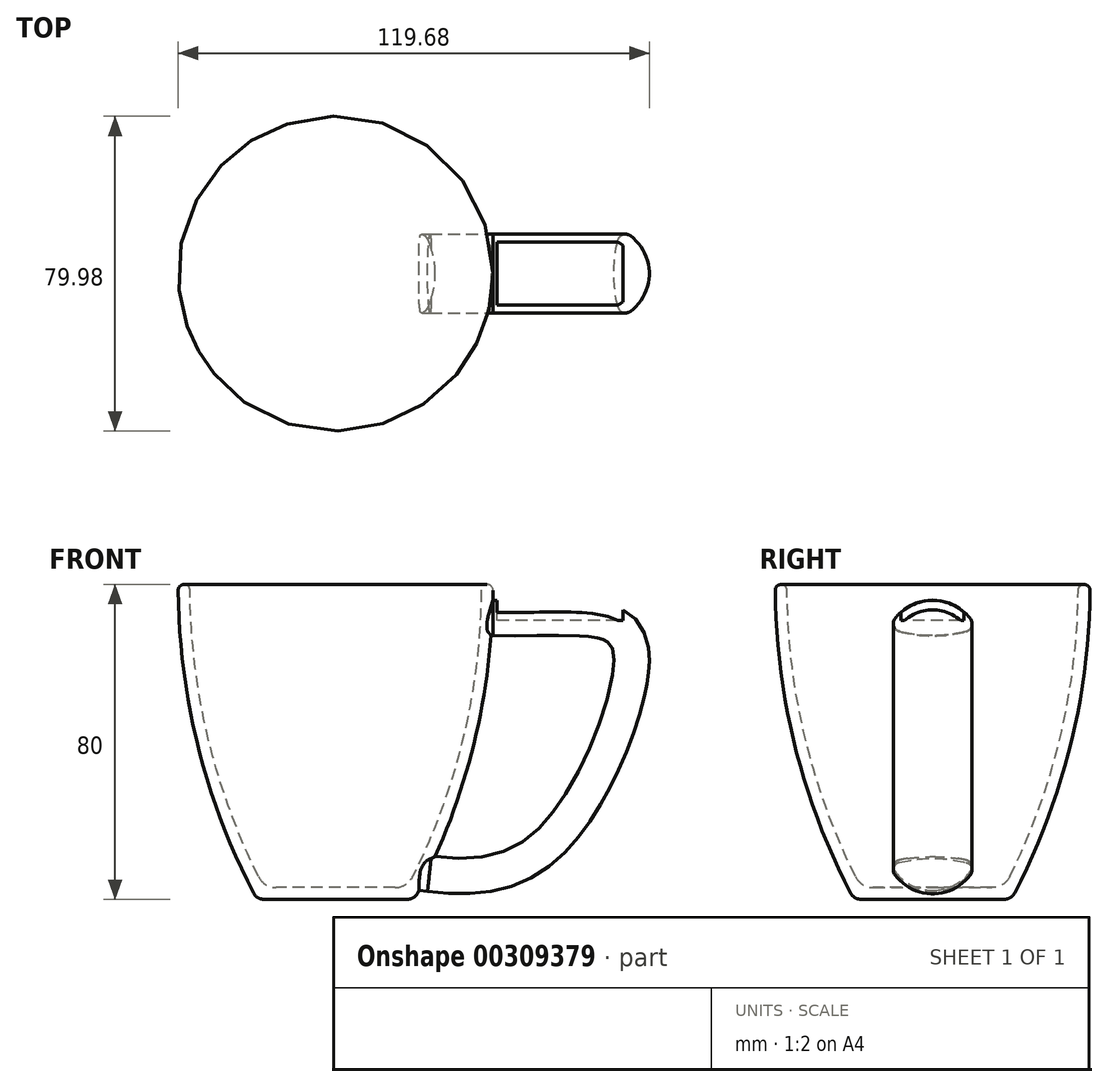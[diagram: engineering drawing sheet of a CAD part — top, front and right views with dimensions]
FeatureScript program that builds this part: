
annotation { "Feature Type Name" : "Feature", "Feature Type Description" : "" }
export const myFeature = defineFeature(function(context is Context, id is Id, definition is map)
    precondition{}
    {
        {
            var Q0;
            Q0=qCreatedBy(makeId("Front.planeOp"),FACE);
            var sketch = newSketch(context, id + "F0", { "sketchPlane" : qUnion([Q0])});
            skLineSegment(sketch, "E0", {"start": v(0, 3) * mm, "end": v(0, 0) * mm});
            skLineSegment(sketch, "E1", {"start": v(0, 0) * mm, "end": v(20, 0) * mm});
            skArc(sketch, "E2", {"start": v(20, 0) * mm, "mid": v(34.92, 38.77) * mm, "end": v(40, 80) * mm});
            skArc(sketch, "E3.0", {"start": v(18.19, 3) * mm, "mid": v(32.23, 40.37) * mm, "end": v(37, 80) * mm});
            skLineSegment(sketch, "E3.1", {"start": v(0, 3) * mm, "end": v(18.19, 3) * mm});
            skLineSegment(sketch, "E4", {"start": v(37, 80) * mm, "end": v(40, 80) * mm});
            skLineSegment(sketch, "E5", {"start": v(40, 160) * mm, "end": v(40, 0) * mm, "construction": true});
            skLineSegment(sketch, "E6", {"start": v(37, 160) * mm, "end": v(37, 0) * mm, "construction": true});
            skSolve(sketch);
        }
        {
            var Q0;
            Q0=qSketchRegion(id+"F0",true);
            var Q1;
            Q1=sQuery(id+"F0.wireOp",EDGE,"E0");
            revolve(context, id + "F1", {"entities" : qUnion([Q0]), "axis" : qUnion([Q1]), "revolveType" : RevolveType.FULL});
        }
        {
            var Q0;
            Q0=sQuery(id+"F0.wireOp",EDGE,"E5");
            cPlane(context, id + "F2", {"entities" : qUnion([Q0]), "cplaneType" : CPlaneType.LINE_ANGLE, "offset" : 150 * mm, "angle" : 0 * degree, "width" : 150 * mm, "height" : 150 * mm});
        }
        {
            var Q0;
            Q0=qCreatedBy(id+"F2.planeOp",FACE);
            var sketch = newSketch(context, id + "F3", { "sketchPlane" : qUnion([Q0])});
            skPoint(sketch, "E7", {"position": v(0, 70) * mm});
            skArc(sketch, "E8", {"start": v(9.6, 71.2) * mm, "mid": v(0, 76) * mm, "end": v(-9.6, 71.2) * mm});
            skArc(sketch, "E9", {"start": v(9.6, 71.2) * mm, "mid": v(9.89, 69.33) * mm, "end": v(8.5, 68.06) * mm});
            skArc(sketch, "E10", {"start": v(-9.6, 71.2) * mm, "mid": v(-9.89, 69.33) * mm, "end": v(-8.5, 68.06) * mm});
            skArc(sketch, "E11", {"start": v(-8.5, 68.06) * mm, "mid": v(0, 67) * mm, "end": v(8.5, 68.06) * mm});
            skSolve(sketch);
        }
        {
            var Q0;
            Q0=qSketchRegion(id+"F3",true);
            extrude(context, id + "F4", {"entities" : qUnion([Q0]), "operationType" : NewBodyOperationType.ADD, "endBound" : BoundingType.UP_TO_NEXT, "depth" : 25 * mm});
        }
        {
            var Q0;
            Q0=qCreatedBy(makeId("Front.planeOp"),FACE);
            var sketch = newSketch(context, id + "F5", { "sketchPlane" : qUnion([Q0])});
            skLineSegment(sketch, "E12", {"start": v(42.52, 70) * mm, "end": v(37.48, 70) * mm, "construction": true});
            skFitSpline(sketch, "E13", {"points": [v(40, 70) * mm, v(67.31, 69.28) * mm, v(73.61, 62.71) * mm, v(57.15, 19.7) * mm, v(24, 8) * mm], "startDerivative": vector(122.83, -3.58) * mm, "endDerivative": vector(-160.62, 21.78) * mm});
            skSolve(sketch);
        }
        {
            var Q0;
            Q0=makeQuery(id+"F3.imprint","IMPRINT",FACE,{"disambiguationData":[TD([[makeQuery(id+"F3.imprint","IMPRINT",EDGE,{"derivedFrom":sQuery(id+"F3.wireOp",EDGE,"E8")}),1.0]])]});
            var Q1;
            Q1=sQuery(id+"F5.wireOp",EDGE,"E13");
            sweep(context, id + "F6", {"operationType" : NewBodyOperationType.ADD, "profiles" : qUnion([Q0]), "path" : qUnion([Q1])});
        }
        {
            var Q0;
            Q0=makeQuery(id+"F1.opRevolve","SWEPT_EDGE",EDGE,{"disambiguationData":[OSD([sQuery(id+"F0.wireOp",EDGE,"E3.0"),sQuery(id+"F0.wireOp",EDGE,"E4")])]});
            var Q1;
            Q1=makeQuery(id+"F1.opRevolve","SWEPT_EDGE",EDGE,{"disambiguationData":[OSD([sQuery(id+"F0.wireOp",EDGE,"E2"),sQuery(id+"F0.wireOp",EDGE,"E4")])]});
            fillet(context, id + "F7", {"entities" : qUnion([Q0, Q1]), "radius" : 1.5 * mm, "tangentPropagation" : true, "allowEdgeOverflow" : false});
        }
        {
            var Q0;
            Q0=makeQuery(id+"F1.opRevolve","SWEPT_EDGE",EDGE,{"disambiguationData":[OSD([sQuery(id+"F0.wireOp",EDGE,"E1"),sQuery(id+"F0.wireOp",EDGE,"E2")])]});
            fillet(context, id + "F8", {"entities" : qUnion([Q0]), "radius" : 3 * mm, "tangentPropagation" : true, "allowEdgeOverflow" : false});
        }
        {
            var Q0;
            Q0=makeQuery(id+"F1.opRevolve","SWEPT_EDGE",EDGE,{"disambiguationData":[OSD([sQuery(id+"F0.wireOp",EDGE,"E3.0"),sQuery(id+"F0.wireOp",EDGE,"E3.1")])]});
            fillet(context, id + "F9", {"entities" : qUnion([Q0]), "radius" : 5 * mm, "tangentPropagation" : true, "allowEdgeOverflow" : false});
        }
        {
            var Q0;
            Q0=makeQuery(id+"F6.opSweep","CAP_FACE",FACE,{"disambiguationData":[OSD([sQuery(id+"F3.wireOp",EDGE,"E8"),sQuery(id+"F3.wireOp",EDGE,"E9"),sQuery(id+"F3.wireOp",EDGE,"E10"),sQuery(id+"F3.wireOp",EDGE,"E11"),sQuery(id+"F5.wireOp",VERTEX,"b8e06edf-8505-42d8-96b9-aa2b29730343.end")])],"isStart":false});
            var sketch = newSketch(context, id + "F10", { "sketchPlane" : qUnion([Q0])});
            skArc(sketch, "E14", {"start": v(8.5, 12.43) * mm, "mid": v(7.47, 12.67) * mm, "end": v(6.43, 12.88) * mm});
            skArc(sketch, "E15", {"start": v(9.6, 9.29) * mm, "mid": v(9.89, 11.15) * mm, "end": v(8.5, 12.43) * mm});
            skArc(sketch, "E16", {"start": v(-9.6, 9.29) * mm, "mid": v(0, 4.49) * mm, "end": v(9.6, 9.29) * mm});
            skArc(sketch, "E17", {"start": v(-8.5, 12.43) * mm, "mid": v(-9.89, 11.15) * mm, "end": v(-9.6, 9.29) * mm});
            skArc(sketch, "E18", {"start": v(-6.43, 12.88) * mm, "mid": v(-7.47, 12.67) * mm, "end": v(-8.5, 12.43) * mm});
            skLineSegment(sketch, "E19", {"start": v(6.43, 12.88) * mm, "end": v(-6.43, 12.88) * mm});
            skSolve(sketch);
        }
        {
            var Q0;
            Q0=qSketchRegion(id+"F10",true);
            var Q1;
            Q1=makeQuery(id+"F1.opRevolve","SWEPT_FACE",FACE,{"disambiguationData":[OSD([sQuery(id+"F0.wireOp",EDGE,"E3.0")])]});
            extrude(context, id + "F11", {"entities" : qUnion([Q0]), "operationType" : NewBodyOperationType.ADD, "endBound" : BoundingType.UP_TO_SURFACE, "endBoundEntityFace" : qUnion([Q1]), "depth" : 25 * mm});
        }
        {
            var Q0;
            Q0=qCreatedBy(makeId("Top.planeOp"),FACE);
            cPlane(context, id + "F12", {"entities" : qUnion([Q0]), "cplaneType" : CPlaneType.OFFSET, "offset" : 74 * mm, "width" : 150 * mm, "height" : 150 * mm});
        }
        {
            var Q0;
            Q0=qCreatedBy(id+"F12.planeOp",FACE);
            var sketch = newSketch(context, id + "F13", { "sketchPlane" : qUnion([Q0])});
            skLineSegment(sketch, "E20.bottom", {"start": v(73, 8) * mm, "end": v(41, 8) * mm});
            skLineSegment(sketch, "E20.top", {"start": v(73, -8) * mm, "end": v(41, -8) * mm});
            skLineSegment(sketch, "E20.left", {"start": v(73, 8) * mm, "end": v(73, -8) * mm});
            skLineSegment(sketch, "E20.right", {"start": v(41, 8) * mm, "end": v(41, -8) * mm});
            skPoint(sketch, "E20.middle", {"position": v(57, 0) * mm});
            skSolve(sketch);
        }
        {
            var Q0;
            Q0=makeQuery(id+"F13.imprint","IMPRINT",FACE,{"disambiguationData":[TD([[makeQuery(id+"F13.imprint","IMPRINT",EDGE,{"derivedFrom":sQuery(id+"F13.wireOp",EDGE,"E20.bottom")}),1.0]])]});
            extrude(context, id + "F14", {"entities" : qUnion([Q0]), "operationType" : NewBodyOperationType.REMOVE, "oppositeDirection" : true, "depth" : 3.2 * mm, "hasSecondDirection" : true, "secondDirectionOppositeDirection" : false, "secondDirectionDepth" : 25 * mm});
        }
    });
